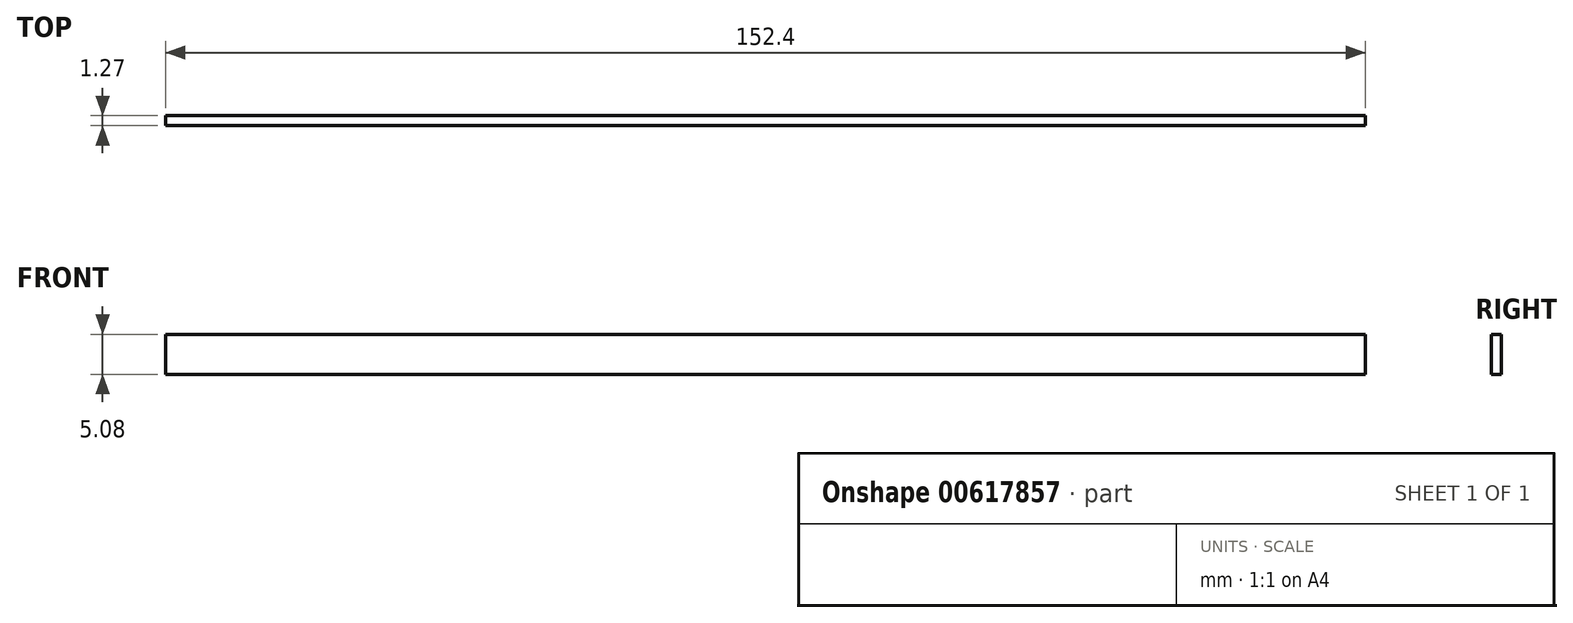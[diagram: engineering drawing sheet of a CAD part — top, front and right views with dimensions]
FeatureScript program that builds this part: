
annotation { "Feature Type Name" : "Feature", "Feature Type Description" : "" }
export const myFeature = defineFeature(function(context is Context, id is Id, definition is map)
    precondition{}
    {
        {
            var Q0;
            Q0=qCreatedBy(makeId("Front.planeOp"),FACE);
            var sketch = newSketch(context, id + "F0", { "sketchPlane" : qUnion([Q0])});
            skLineSegment(sketch, "E0.bottom", {"start": v(-25.66, 3.17) * mm, "end": v(126.74, 3.17) * mm});
            skLineSegment(sketch, "E0.top", {"start": v(-25.66, -1.9) * mm, "end": v(126.74, -1.9) * mm});
            skLineSegment(sketch, "E0.left", {"start": v(-25.66, 3.17) * mm, "end": v(-25.66, -1.9) * mm});
            skLineSegment(sketch, "E0.right", {"start": v(126.74, 3.17) * mm, "end": v(126.74, -1.9) * mm});
            skSolve(sketch);
        }
        {
            var Q0;
            Q0 = qSketchRegion(id + "F0", true);
            extrude(context, id + "F1", {"entities" : qUnion([Q0]), "depth" : 1.27 * mm, "offsetDistance" : 25.4 * mm});
        }
    });
